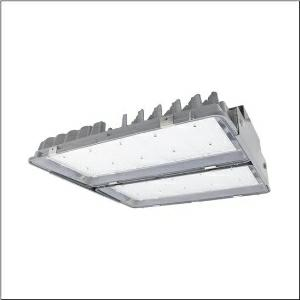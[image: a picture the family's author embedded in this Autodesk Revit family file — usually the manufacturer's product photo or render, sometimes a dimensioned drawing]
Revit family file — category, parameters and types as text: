
# Revit family: highbay_11xtreme_51hf81db4wma
name_source: partatom
category: Lighting Fixtures
units: mm (PartAtom-declared; Revit-internal decimal feet)

## family parameters
Cut with Voids When Loaded = No
Host = Face
Light Source = No
Part Type = Normal
Room Calculation Point = No
Round Connector Dimension = Use Diameter
Shared = No

## types (1)
- --- (1 x LED, 76000 lm, 422.2 W, 4000K)
    Apparent Load = 422 VA
    CIE Flux Codes = 88 96 99 100 100
    Color Rendering = 80
    Color Temperature = 4000K
    Default Elevation = 1800 mm
    Description = Highbay 11Xtreme, high bay luminaire, primary light control with lens, of PMMA, primary optical cover: cover, of toughened safety glass, light emission: direct distribution, primary light characteristic: symmetric, installation type: suspended mounting, surface-mounted, 2x LED module,for 1x 2x LED, rated luminous flux: 76.000lm, luminous efficacy: 180lm/W, light colour: 840, colour temperature: 4000K, control gear: DALI 2 (with two DALI addresses), with cable H07RN-F 5x 1.5mm², mains connection: 220..240V, AC, 50/60Hz, cable length: 1,5m, rated input power: 422W, luminaire housing, of diecast aluminium, partly coated, silver, length: 595mm, width: 560mm, height: 195mm, protection rating (complete): IP66, insulation class (complete): insulation class I (protective earthing), certification: CE, ENEC, UKCA, protection symbol: D, ball protection: ball impact resistant according to DIN VDE 0710 part 13 (with chain suspension), impact resistance: IK08, permissible operating ambient temperature: -25..+45°C, reducing of maximum allowable ambient temperature of 5°C with ceiling mounting, packaging unit: 1 piece
    Height = 157 mm
    Lamp = 1 x LED
    Lamp Light Flux = 76000 lm
    Lamp Power = 422.2 W
    Lamp count = 1
    Length = 593 mm
    Luminous efficacy = 180 lm/W
    Manufacturer = Siteco
    ModVariant = No
    Model = 51HF81DB4WMA
    Mounting Place = Ceiling
    Mounting Type = Pendant
    Number of Poles = 1
    OnlyDefault = Yes
    Power Factor = 1
    Product Name = Highbay 11Xtreme
    Product group = high bay luminaire
    ProductGroupID = 902
    Protection Class = Protection class I
    Protection Degree = IP 66
    RLX_Detail_Level = 1
    RLX_Emergency_Light_Flux = 0 lm
    RLX_Emergency_Type = 0
    RLX_Emergency_Type_DB = No
    RlxData = <blob elided: 33873 chars, md5=15611ff0>
    Socket = socket
    Standby Power = 0 W
    System Light Flux = 76000 lm
    System Power = 422 W
    Type Comments = factory setting: luminous flux: 100 % | dim-lin: 254 | 1389 mA
    Type Image = l_1258340.jpg
    URL = http://relux.com
    VarID = @adj_088659
    Voltage = 0 V
    Weight = 0.00 kg
    Width = 278 mm

## geometry (parser evidence)
native form markers: Blend x4, Sweep x9
no freeform markers — native parametric forms only
